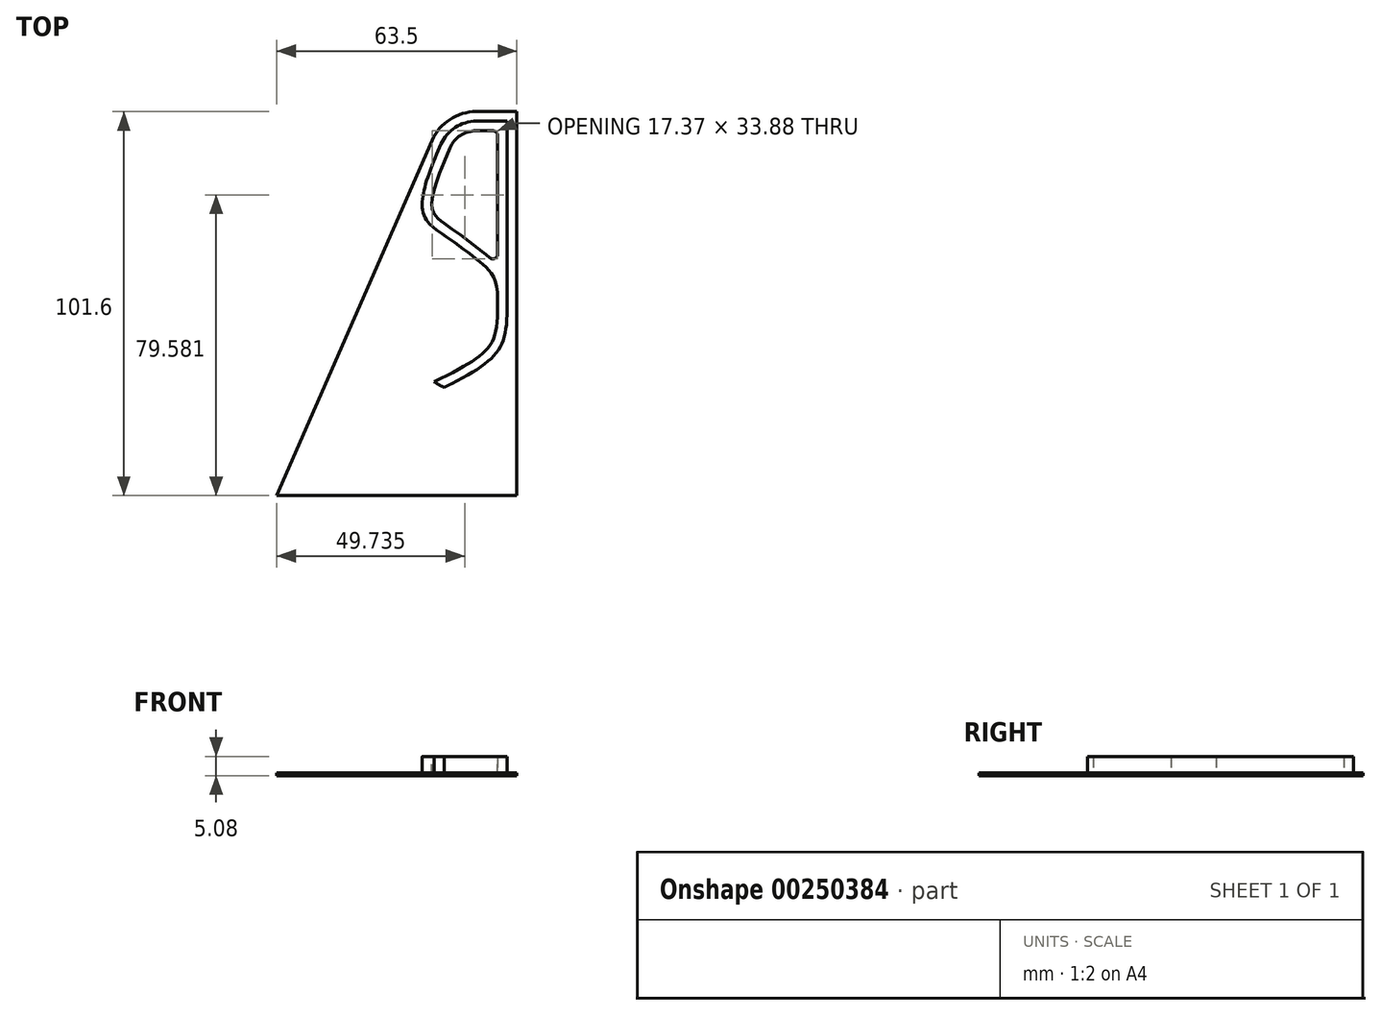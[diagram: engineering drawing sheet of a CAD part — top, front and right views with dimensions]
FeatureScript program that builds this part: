
annotation { "Feature Type Name" : "Feature", "Feature Type Description" : "" }
export const myFeature = defineFeature(function(context is Context, id is Id, definition is map)
    precondition{}
    {
        {
            var Q0;
            Q0=qCreatedBy(makeId("Top.planeOp"),FACE);
            var sketch = newSketch(context, id + "F0", { "sketchPlane" : qUnion([Q0])});
            skLineSegment(sketch, "E0", {"start": v(0, 0) * mm, "end": v(-63.5, 0) * mm});
            skLineSegment(sketch, "E1", {"start": v(-63.5, 0) * mm, "end": v(-22.38, 94) * mm});
            skLineSegment(sketch, "E2", {"start": v(-10.74, 101.6) * mm, "end": v(0, 101.6) * mm});
            skLineSegment(sketch, "E3", {"start": v(0, 101.6) * mm, "end": v(0, 0) * mm});
            skPoint(sketch, "E4.visualSharp", {"position": v(-19.05, 101.6) * mm});
            skArc(sketch, "E4.filletArc", {"start": v(-10.74, 101.6) * mm, "mid": v(-17.7, 99.53) * mm, "end": v(-22.38, 94) * mm});
            skSolve(sketch);
        }
        {
            var Q0;
            Q0=makeQuery(id+"F0.imprint","IMPRINT",FACE,{"disambiguationData":[TD([[makeQuery(id+"F0.imprint","IMPRINT",EDGE,{"derivedFrom":sQuery(id+"F0.wireOp",EDGE,"E0")}),-1.0]])]});
            extrude(context, id + "F1", {"entities" : qUnion([Q0]), "depth" : 0.76 * mm});
        }
        {
            var Q0;
            Q0=qCreatedBy(makeId("Top.planeOp"),FACE);
            var sketch = newSketch(context, id + "F2", { "sketchPlane" : qUnion([Q0])});
            skArc(sketch, "E5.1", {"start": v(-10.74, 96.52) * mm, "mid": v(-14.91, 95.28) * mm, "end": v(-17.73, 91.95) * mm});
            skLineSegment(sketch, "E6", {"start": v(0, 5.08) * mm, "end": v(-2.54, 5.08) * mm, "construction": true});
            skPoint(sketch, "E7", {"position": v(-2.54, 5.08) * mm});
            skPoint(sketch, "E8", {"position": v(-55.73, 5.08) * mm});
            skPoint(sketch, "E9", {"position": v(-2.54, 96.52) * mm});
            skFitSpline(sketch, "E10", {"points": [v(-55.73, 5.08) * mm, v(-42.65, 18.44) * mm, v(-8.65, 34.72) * mm, v(-2.54, 50.8) * mm], "startDerivative": vector(38.78, 88.63) * mm, "endDerivative": vector(0, 89.88) * mm});
            skFitSpline(sketch, "E11", {"points": [v(-35.73, 50.8) * mm, v(-30.69, 35.13) * mm, v(-9.87, 22.94) * mm, v(-2.54, 5.08) * mm], "startDerivative": vector(-43.24, -98.84) * mm, "endDerivative": vector(0, -112.43) * mm});
            skFitSpline(sketch, "E12", {"points": [v(-17.73, 91.95) * mm, v(-19, 71.85) * mm, v(-7.67, 63.36) * mm, v(-2.54, 50.8) * mm], "startDerivative": vector(-55.83, -127.6) * mm, "endDerivative": vector(0, -74.13) * mm});
            skFitSpline(sketch, "E13.0", {"points": [v(-20.05, 92.97) * mm, v(-21.23, 90.28) * mm, v(-22.64, 86.84) * mm, v(-23.9, 83.17) * mm, v(-24.55, 80.8) * mm, v(-24.93, 78.74) * mm, v(-25.04, 76.9) * mm, v(-24.85, 75.18) * mm, v(-24.3, 73.62) * mm, v(-23.47, 72.32) * mm, v(-22.49, 71.3) * mm, v(-21.66, 70.64) * mm, v(-21, 70.16) * mm, v(-20.51, 69.8) * mm, v(-20.02, 69.46) * mm, v(-19.33, 68.97) * mm, v(-18.43, 68.32) * mm, v(-17.3, 67.51) * mm, v(-16.14, 66.67) * mm, v(-14.95, 65.8) * mm, v(-13.77, 64.93) * mm, v(-12.61, 64.05) * mm, v(-11.48, 63.18) * mm, v(-10.41, 62.33) * mm, v(-9.58, 61.64) * mm, v(-8.96, 61.12) * mm, v(-8.39, 60.62) * mm, v(-7.76, 60.03) * mm, v(-7.14, 59.34) * mm, v(-6.63, 58.65) * mm, v(-6.2, 57.9) * mm, v(-5.83, 57) * mm, v(-5.51, 55.9) * mm, v(-5.2, 54.08) * mm, v(-5.08, 52.26) * mm, v(-5.08, 50.8) * mm]});
            skFitSpline(sketch, "E14.0", {"points": [v(-38.06, 51.82) * mm, v(-38.54, 50.72) * mm, v(-39.32, 48.66) * mm, v(-40.02, 45.89) * mm, v(-40.22, 43.35) * mm, v(-39.91, 41.01) * mm, v(-39.09, 38.94) * mm, v(-37.87, 37.21) * mm, v(-36.4, 35.82) * mm, v(-34.83, 34.66) * mm, v(-33.45, 33.8) * mm, v(-32.33, 33.15) * mm, v(-31.2, 32.5) * mm, v(-29.74, 31.65) * mm, v(-27.92, 30.61) * mm, v(-26.05, 29.55) * mm, v(-23.53, 28.12) * mm, v(-20.37, 26.32) * mm, v(-17.32, 24.54) * mm, v(-15.03, 23.18) * mm, v(-13.41, 22.19) * mm, v(-11.9, 21.24) * mm, v(-10.54, 20.35) * mm, v(-9.39, 19.53) * mm, v(-8.44, 18.75) * mm, v(-7.68, 17.97) * mm, v(-7.04, 17.1) * mm, v(-6.5, 16.07) * mm, v(-6, 14.74) * mm, v(-5.6, 13.05) * mm, v(-5.2, 10.2) * mm, v(-5.08, 7.36) * mm, v(-5.08, 5.08) * mm]});
            skFitSpline(sketch, "E15.0", {"points": [v(-58.06, 6.1) * mm, v(-57.23, 8) * mm, v(-56.03, 10.43) * mm, v(-54.36, 13.05) * mm, v(-53.03, 14.74) * mm, v(-51.6, 16.2) * mm, v(-50.04, 17.43) * mm, v(-48.38, 18.5) * mm, v(-46.6, 19.44) * mm, v(-45, 20.18) * mm, v(-43.62, 20.8) * mm, v(-42.17, 21.42) * mm, v(-40.22, 22.25) * mm, v(-36.86, 23.66) * mm, v(-32.3, 25.56) * mm, v(-26.6, 28) * mm, v(-21, 30.55) * mm, v(-16.72, 32.7) * mm, v(-13.7, 34.4) * mm, v(-11.7, 35.65) * mm, v(-10, 36.85) * mm, v(-8.65, 37.98) * mm, v(-7.62, 39.07) * mm, v(-6.84, 40.14) * mm, v(-6.25, 41.29) * mm, v(-5.79, 42.6) * mm, v(-5.45, 44.14) * mm, v(-5.15, 46.61) * mm, v(-5.08, 48.97) * mm, v(-5.08, 50.8) * mm]});
            skLineSegment(sketch, "E16", {"start": v(-20.05, 92.97) * mm, "end": v(-59.62, 2.54) * mm});
            skLineSegment(sketch, "E17", {"start": v(-59.62, 2.54) * mm, "end": v(-2.54, 2.54) * mm});
            skLineSegment(sketch, "E18", {"start": v(-2.54, 2.54) * mm, "end": v(-2.54, 5.08) * mm});
            skLineSegment(sketch, "E19", {"start": v(-53.76, 5.08) * mm, "end": v(-6.36, 5.08) * mm});
            skPoint(sketch, "E20", {"position": v(-39.89, 41.3) * mm});
            skPoint(sketch, "E21", {"position": v(-50.5, 17.06) * mm});
            skLineSegment(sketch, "E22", {"start": v(-41.1, 38.53) * mm, "end": v(-48.86, 20.8) * mm});
            skPoint(sketch, "E23", {"position": v(-24.87, 75.62) * mm});
            skLineSegment(sketch, "E24", {"start": v(-35.73, 50.8) * mm, "end": v(-26.94, 70.89) * mm});
            skLineSegment(sketch, "E25", {"start": v(-2.54, 50.8) * mm, "end": v(-2.54, 96.52) * mm});
            skPoint(sketch, "E26.endSnap0", {"position": v(-17.7, 99.53) * mm});
            skArc(sketch, "E27.0", {"start": v(-10.74, 99.06) * mm, "mid": v(-16.3, 97.4) * mm, "end": v(-20.05, 92.97) * mm});
            skLineSegment(sketch, "E28", {"start": v(-10.74, 99.06) * mm, "end": v(-2.54, 99.06) * mm});
            skLineSegment(sketch, "E29", {"start": v(-2.54, 99.06) * mm, "end": v(-2.54, 96.52) * mm});
            skLineSegment(sketch, "E30", {"start": v(-6.35, 96.52) * mm, "end": v(-10.74, 96.52) * mm});
            skLineSegment(sketch, "E31", {"start": v(-5.08, 95.25) * mm, "end": v(-5.08, 63.9) * mm});
            skFitSpline(sketch, "E32.trimOffspring", {"points": [v(-58.06, 6.1) * mm, v(-57.23, 8) * mm, v(-56.03, 10.43) * mm, v(-54.36, 13.05) * mm, v(-53.03, 14.74) * mm, v(-51.6, 16.2) * mm, v(-50.04, 17.43) * mm, v(-48.38, 18.5) * mm, v(-46.6, 19.44) * mm, v(-45, 20.18) * mm, v(-43.62, 20.8) * mm, v(-42.17, 21.42) * mm, v(-40.22, 22.25) * mm, v(-36.86, 23.66) * mm, v(-32.3, 25.56) * mm, v(-26.6, 28) * mm, v(-21, 30.55) * mm, v(-16.72, 32.7) * mm, v(-13.7, 34.4) * mm, v(-11.7, 35.65) * mm, v(-10, 36.85) * mm, v(-8.65, 37.98) * mm, v(-7.62, 39.07) * mm, v(-6.84, 40.14) * mm, v(-6.25, 41.29) * mm, v(-5.79, 42.6) * mm, v(-5.45, 44.14) * mm, v(-5.15, 46.61) * mm, v(-5.08, 48.97) * mm, v(-5.08, 50.8) * mm]});
            skFitSpline(sketch, "E33.trimOffspring", {"points": [v(-38.06, 51.82) * mm, v(-38.54, 50.72) * mm, v(-39.32, 48.66) * mm, v(-40.02, 45.89) * mm, v(-40.22, 43.35) * mm, v(-39.91, 41.01) * mm, v(-39.09, 38.94) * mm, v(-37.87, 37.21) * mm, v(-36.4, 35.82) * mm, v(-34.83, 34.66) * mm, v(-33.45, 33.8) * mm, v(-32.33, 33.15) * mm, v(-31.2, 32.5) * mm, v(-29.74, 31.65) * mm, v(-27.92, 30.61) * mm, v(-26.05, 29.55) * mm, v(-23.53, 28.12) * mm, v(-20.37, 26.32) * mm, v(-17.32, 24.54) * mm, v(-15.03, 23.18) * mm, v(-13.41, 22.19) * mm, v(-11.9, 21.24) * mm, v(-10.54, 20.35) * mm, v(-9.39, 19.53) * mm, v(-8.44, 18.75) * mm, v(-7.68, 17.97) * mm, v(-7.04, 17.1) * mm, v(-6.5, 16.07) * mm, v(-6, 14.74) * mm, v(-5.6, 13.05) * mm, v(-5.2, 10.2) * mm, v(-5.08, 7.36) * mm, v(-5.08, 5.08) * mm]});
            skArc(sketch, "E34.filletArc", {"start": v(-22.82, 71.66) * mm, "mid": v(-25.08, 72.36) * mm, "end": v(-26.94, 70.89) * mm});
            skPoint(sketch, "E35.visualSharp", {"position": v(-21.95, 30.14) * mm});
            skArc(sketch, "E35.filletArc", {"start": v(-23.1, 30.8) * mm, "mid": v(-21.93, 30.47) * mm, "end": v(-20.75, 30.71) * mm});
            skPoint(sketch, "E36.visualSharp", {"position": v(-5.08, 60.82) * mm});
            skArc(sketch, "E36.filletArc", {"start": v(-7.18, 62.94) * mm, "mid": v(-5.82, 62.74) * mm, "end": v(-5.08, 63.9) * mm});
            skPoint(sketch, "E37.visualSharp", {"position": v(-5.08, 96.52) * mm});
            skArc(sketch, "E37.filletArc", {"start": v(-5.08, 95.25) * mm, "mid": v(-5.45, 96.15) * mm, "end": v(-6.35, 96.52) * mm});
            skPoint(sketch, "E38.visualSharp", {"position": v(-5.08, 5.08) * mm});
            skArc(sketch, "E38.filletArc", {"start": v(-6.36, 5.08) * mm, "mid": v(-5.45, 5.46) * mm, "end": v(-5.09, 6.37) * mm});
            skArc(sketch, "E39.filletArc", {"start": v(-54.9, 6.9) * mm, "mid": v(-54.83, 5.67) * mm, "end": v(-53.76, 5.08) * mm});
            skArc(sketch, "E40.filletArc", {"start": v(-48.86, 20.8) * mm, "mid": v(-48.56, 19.36) * mm, "end": v(-47.11, 19.15) * mm});
            skArc(sketch, "E41.filletArc", {"start": v(-38.84, 38.67) * mm, "mid": v(-40.01, 39.3) * mm, "end": v(-41.1, 38.53) * mm});
            skPoint(sketch, "E42.visualSharp", {"position": v(-24.8, 28.83) * mm});
            skArc(sketch, "E42.filletArc", {"start": v(-27.1, 27.81) * mm, "mid": v(-26.34, 28.9) * mm, "end": v(-26.98, 30.08) * mm});
            skPoint(sketch, "E43.visualSharp", {"position": v(-19.27, 28.6) * mm});
            skArc(sketch, "E43.filletArc", {"start": v(-17.16, 29.65) * mm, "mid": v(-17.86, 28.56) * mm, "end": v(-17.23, 27.42) * mm});
            skSolve(sketch);
        }
        {
            var Q0;
            Q0=makeQuery(id+"F2.imprint","IMPRINT",FACE,{"disambiguationData":[TD([[makeQuery(id+"F2.imprint","IMPRINT",EDGE,{"derivedFrom":sQuery(id+"F2.wireOp",EDGE,"E5.1")}),-1.0]])]});
            extrude(context, id + "F3", {"entities" : qUnion([Q0]), "depth" : 5.08 * mm});
        }
    });
